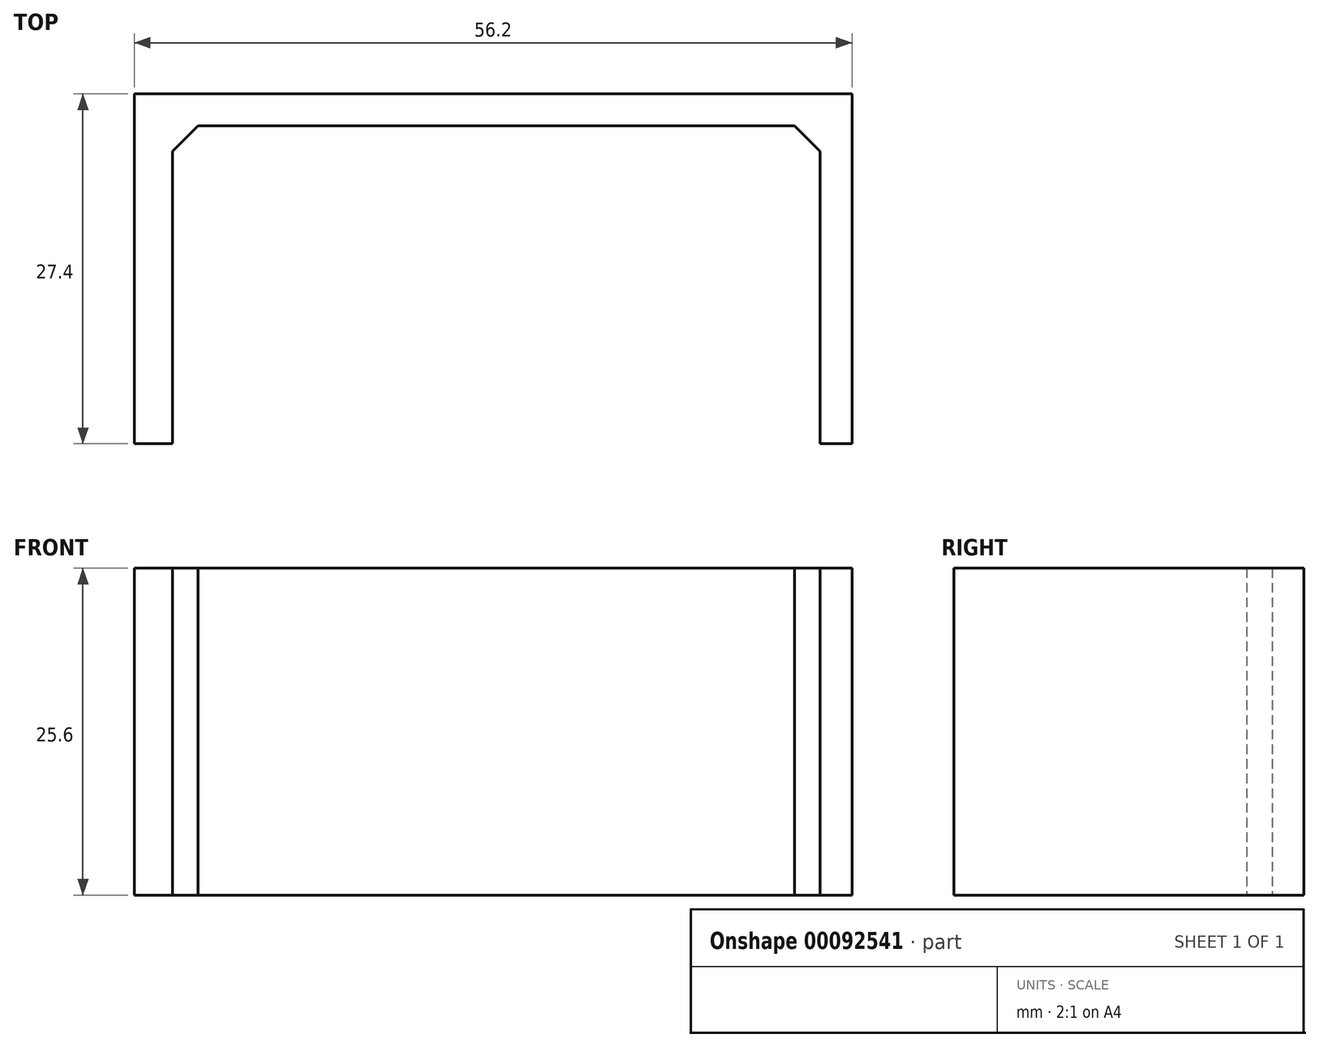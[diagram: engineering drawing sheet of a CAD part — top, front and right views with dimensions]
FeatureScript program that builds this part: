
annotation { "Feature Type Name" : "Feature", "Feature Type Description" : "" }
export const myFeature = defineFeature(function(context is Context, id is Id, definition is map)
    precondition{}
    {
        {
            var Q0;
            Q0=qCreatedBy(makeId("Top.planeOp"),FACE);
            var sketch = newSketch(context, id + "F0", { "sketchPlane" : qUnion([Q0])});
            skLineSegment(sketch, "E0.bottom", {"start": v(0, 0) * mm, "end": v(56.2, 0) * mm});
            skLineSegment(sketch, "E0.top", {"start": v(0, -27.4) * mm, "end": v(56.2, -27.4) * mm});
            skLineSegment(sketch, "E0.left", {"start": v(0, 0) * mm, "end": v(0, -27.4) * mm});
            skLineSegment(sketch, "E0.right", {"start": v(56.2, 0) * mm, "end": v(56.2, -27.4) * mm});
            skLineSegment(sketch, "E1.bottom", {"start": v(3, -2.5) * mm, "end": v(53.7, -2.5) * mm});
            skLineSegment(sketch, "E1.top", {"start": v(3, -27.4) * mm, "end": v(53.7, -27.4) * mm});
            skLineSegment(sketch, "E1.left", {"start": v(3, -2.5) * mm, "end": v(3, -27.4) * mm});
            skLineSegment(sketch, "E1.right", {"start": v(53.7, -2.5) * mm, "end": v(53.7, -27.4) * mm});
            skLineSegment(sketch, "E2", {"start": v(3, -4.5) * mm, "end": v(5, -2.5) * mm});
            skLineSegment(sketch, "E3", {"start": v(51.7, -2.5) * mm, "end": v(53.7, -4.5) * mm});
            skSolve(sketch);
        }
        {
            var Q0;
            Q0=makeQuery(id+"F0.imprint","IMPRINT",FACE,{"disambiguationData":[TD([[makeQuery(id+"F0.imprint","IMPRINT",EDGE,{"derivedFrom":sQuery(id+"F0.wireOp",EDGE,"E0.bottom")}),-1.0]])]});
            var Q1;
            {var subQ0=sQuery(id+"F0.wireOp",EDGE,"E3");Q1=makeQuery(id+"F0.imprint","IMPRINT",FACE,{"disambiguationData":[TD([[makeQuery(id+"F0.imprint","IMPRINT",EDGE,{"derivedFrom":subQ0}),1.0]])]});}
            var Q2;
            {var subQ0=sQuery(id+"F0.wireOp",EDGE,"E2");Q2=makeQuery(id+"F0.imprint","IMPRINT",FACE,{"disambiguationData":[TD([[makeQuery(id+"F0.imprint","IMPRINT",EDGE,{"derivedFrom":subQ0}),1.0]])]});}
            extrude(context, id + "F1", {"entities" : qUnion([Q0, Q1, Q2]), "depth" : 25.6 * mm, "offsetDistance" : 25 * mm});
        }
    });
